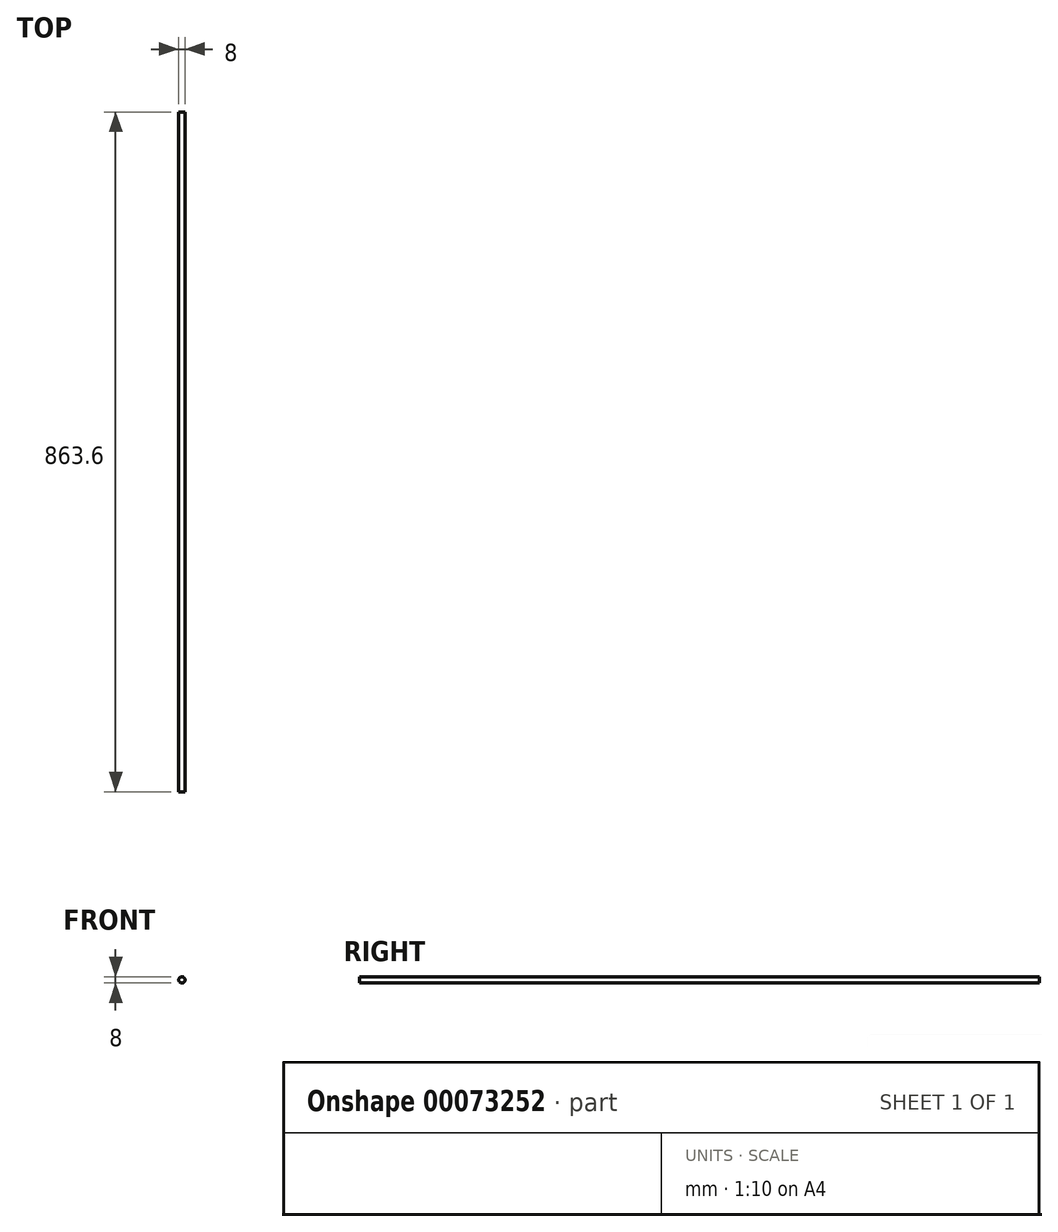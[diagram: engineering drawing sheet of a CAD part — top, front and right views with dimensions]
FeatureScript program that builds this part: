
annotation { "Feature Type Name" : "Feature", "Feature Type Description" : "" }
export const myFeature = defineFeature(function(context is Context, id is Id, definition is map)
    precondition{}
    {
        {
            var Q0;
            Q0=qCreatedBy(makeId("Front.planeOp"),FACE);
            var sketch = newSketch(context, id + "F0", { "sketchPlane" : qUnion([Q0])});
            skCircle(sketch, "E0", {"center": v(0, 0) * mm, "radius": 4 * mm});
            skSolve(sketch);
        }
        {
            var Q0;
            Q0=makeQuery(id+"F0.imprint","IMPRINT",FACE,{"disambiguationData":[TD([[makeQuery(id+"F0.imprint","IMPRINT",EDGE,{"derivedFrom":sQuery(id+"F0.wireOp",EDGE,"E0")}),1.0]])]});
            extrude(context, id + "F1", {"entities" : qUnion([Q0]), "depth" : 863.6 * mm});
        }
    });
